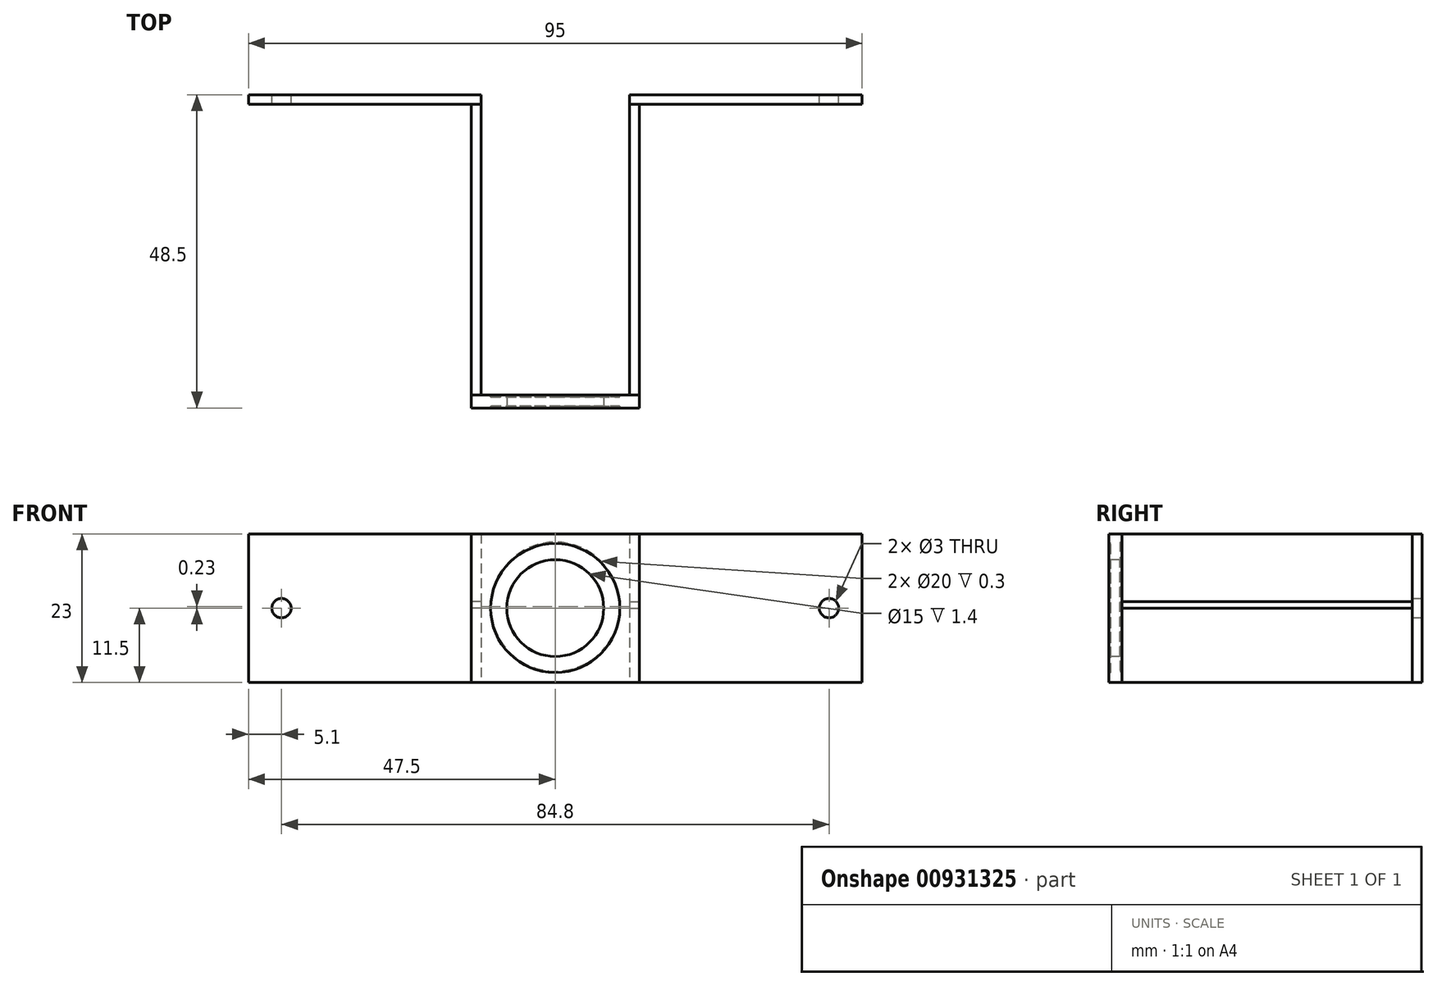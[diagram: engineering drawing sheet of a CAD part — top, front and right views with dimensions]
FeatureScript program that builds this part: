
annotation { "Feature Type Name" : "Feature", "Feature Type Description" : "" }
export const myFeature = defineFeature(function(context is Context, id is Id, definition is map)
    precondition{}
    {
        {
            var Q0;
            Q0=qCreatedBy(makeId("Front.planeOp"),FACE);
            var sketch = newSketch(context, id + "F0", { "sketchPlane" : qUnion([Q0])});
            skLineSegment(sketch, "E0.bottom", {"start": v(-47.5, 11.5) * mm, "end": v(47.5, 11.5) * mm});
            skLineSegment(sketch, "E0.top", {"start": v(-47.5, -11.5) * mm, "end": v(47.5, -11.5) * mm});
            skLineSegment(sketch, "E0.left", {"start": v(-47.5, 11.5) * mm, "end": v(-47.5, -11.5) * mm});
            skLineSegment(sketch, "E0.right", {"start": v(47.5, 11.5) * mm, "end": v(47.5, -11.5) * mm});
            skPoint(sketch, "E0.middle", {"position": v(0, 0) * mm});
            skCircle(sketch, "E1", {"center": v(-42.4, 0) * mm, "radius": 1.5 * mm});
            skCircle(sketch, "E2", {"center": v(42.4, 0) * mm, "radius": 1.5 * mm});
            skLineSegment(sketch, "E3.bottom", {"start": v(-11.5, 11.5) * mm, "end": v(11.5, 11.5) * mm});
            skLineSegment(sketch, "E3.top", {"start": v(-11.5, -11.5) * mm, "end": v(11.5, -11.5) * mm});
            skLineSegment(sketch, "E3.left", {"start": v(-11.5, 11.5) * mm, "end": v(-11.5, -11.5) * mm});
            skLineSegment(sketch, "E3.right", {"start": v(11.5, 11.5) * mm, "end": v(11.5, -11.5) * mm});
            skSolve(sketch);
        }
        {
            var Q0;
            {var subQ0=sQuery(id+"F0.wireOp",EDGE,"E0.left");Q0=makeQuery(id+"F0.imprint","IMPRINT",FACE,{"disambiguationData":[TD([[makeQuery(id+"F0.imprint","IMPRINT",EDGE,{"derivedFrom":subQ0}),1.0]])]});}
            var Q1;
            {var subQ0=sQuery(id+"F0.wireOp",EDGE,"E0.right");Q1=makeQuery(id+"F0.imprint","IMPRINT",FACE,{"disambiguationData":[TD([[makeQuery(id+"F0.imprint","IMPRINT",EDGE,{"derivedFrom":subQ0}),-1.0]])]});}
            extrude(context, id + "F1", {"entities" : qUnion([Q0, Q1]), "depth" : 1.5 * mm, "offsetDistance" : 25 * mm});
        }
        {
            var Q0;
            Q0=qCreatedBy(makeId("Top.planeOp"),FACE);
            var sketch = newSketch(context, id + "F2", { "sketchPlane" : qUnion([Q0])});
            skLineSegment(sketch, "E4.bottom", {"start": v(-11.5, -1.5) * mm, "end": v(-13, -1.5) * mm});
            skLineSegment(sketch, "E4.top", {"start": v(-11.5, -46.5) * mm, "end": v(-13, -46.5) * mm});
            skLineSegment(sketch, "E4.left", {"start": v(-11.5, -1.5) * mm, "end": v(-11.5, -46.5) * mm});
            skLineSegment(sketch, "E4.right", {"start": v(-13, -1.5) * mm, "end": v(-13, -46.5) * mm});
            skLineSegment(sketch, "E5.bottom", {"start": v(11.5, -1.5) * mm, "end": v(13, -1.5) * mm});
            skLineSegment(sketch, "E5.top", {"start": v(11.5, -46.5) * mm, "end": v(13, -46.5) * mm});
            skLineSegment(sketch, "E5.left", {"start": v(11.5, -1.5) * mm, "end": v(11.5, -46.5) * mm});
            skLineSegment(sketch, "E5.right", {"start": v(13, -1.5) * mm, "end": v(13, -46.5) * mm});
            skSolve(sketch);
        }
        {
            var Q0;
            Q0=makeQuery(id+"F2.imprint","IMPRINT",FACE,{"disambiguationData":[TD([[makeQuery(id+"F2.imprint","IMPRINT",EDGE,{"derivedFrom":sQuery(id+"F2.wireOp",EDGE,"E5.bottom")}),-1.0]])]});
            var Q1;
            Q1=makeQuery(id+"F2.imprint","IMPRINT",FACE,{"disambiguationData":[TD([[makeQuery(id+"F2.imprint","IMPRINT",EDGE,{"derivedFrom":sQuery(id+"F2.wireOp",EDGE,"E4.bottom")}),1.0]])]});
            extrude(context, id + "F3", {"entities" : qUnion([Q0, Q1]), "endBound" : BoundingType.SYMMETRIC, "depth" : 23 * mm, "offsetDistance" : 25 * mm});
        }
        {
            var Q0;
            Q0 = qSketchRegion(id + "F2", true);
            extrude(context, id + "F4", {"entities" : qUnion([Q0]), "depth" : 1 * mm, "offsetDistance" : 25 * mm});
        }
        {
            var Q0;
            Q0=makeQuery(id+"F3.opExtrude","SWEPT_FACE",FACE,{"disambiguationData":[OSD([sQuery(id+"F2.wireOp",EDGE,"E5.top")])]});
            var sketch = newSketch(context, id + "F5", { "sketchPlane" : qUnion([Q0])});
            skLineSegment(sketch, "E6.bottom", {"start": v(13, 11.5) * mm, "end": v(-13, 11.5) * mm});
            skLineSegment(sketch, "E6.top", {"start": v(13, -11.5) * mm, "end": v(-13, -11.5) * mm});
            skLineSegment(sketch, "E6.left", {"start": v(13, 11.5) * mm, "end": v(13, -11.5) * mm});
            skLineSegment(sketch, "E6.right", {"start": v(-13, 11.5) * mm, "end": v(-13, -11.5) * mm});
            skSolve(sketch);
        }
        {
            var Q0;
            Q0=makeQuery(id+"F5.imprint","IMPRINT",FACE,{"disambiguationData":[TD([[makeQuery(id+"F5.imprint","IMPRINT",EDGE,{"derivedFrom":sQuery(id+"F5.wireOp",EDGE,"E6.top")}),-1.0]])]});
            var Q1;
            {var subQ3=sQuery(id+"F5.wireOp",EDGE,"E6.left");Q1=makeQuery(id+"F5.imprint","IMPRINT",FACE,{"disambiguationData":[TD([[makeQuery(id+"F5.imprint","IMPRINT",EDGE,{"derivedFrom":subQ3}),-1.0]])]});}
            extrude(context, id + "F6", {"entities" : qUnion([Q0, Q1]), "depth" : 2 * mm, "offsetDistance" : 25 * mm});
        }
        {
            var Q0;
            Q0=makeQuery(id+"F6.opExtrude","CAP_FACE",FACE,{"disambiguationData":[OSD([sQuery(id+"F5.wireOp",EDGE,"E6.bottom"),sQuery(id+"F5.wireOp",EDGE,"E6.top"),sQuery(id+"F5.wireOp",EDGE,"E6.left"),sQuery(id+"F5.wireOp",EDGE,"E6.right")])],"isStart":false});
            var sketch = newSketch(context, id + "F7", { "sketchPlane" : qUnion([Q0])});
            skCircle(sketch, "E7", {"center": v(0, 0) * mm, "radius": 7.5 * mm});
            skCircle(sketch, "E8", {"center": v(0, 0) * mm, "radius": 10 * mm});
            skSolve(sketch);
        }
        {
            var Q0;
            Q0=makeQuery(id+"F7.imprint","IMPRINT",FACE,{"disambiguationData":[TD([[makeQuery(id+"F7.imprint","IMPRINT",EDGE,{"derivedFrom":sQuery(id+"F7.wireOp",EDGE,"E7")}),-1.0]])]});
            extrude(context, id + "F8", {"entities" : qUnion([Q0]), "operationType" : NewBodyOperationType.REMOVE, "oppositeDirection" : true, "depth" : .3 * mm, "offsetDistance" : 25 * mm});
        }
        {
            var Q0;
            Q0=makeQuery(id+"F8.boolean.opBoolean","SPLIT",FACE,{"disambiguationData":[TD([makeQuery(id+"F8.opExtrude","SWEPT_FACE",FACE,{"disambiguationData":[OSD([sQuery(id+"F7.wireOp",EDGE,"E7")])]})])],"derivedFrom":makeQuery(id+"F6.opExtrude","CAP_FACE",FACE,{"disambiguationData":[OSD([sQuery(id+"F5.wireOp",EDGE,"E6.bottom"),sQuery(id+"F5.wireOp",EDGE,"E6.top"),sQuery(id+"F5.wireOp",EDGE,"E6.left"),sQuery(id+"F5.wireOp",EDGE,"E6.right")])],"isStart":false})});
            extrude(context, id + "F9", {"entities" : qUnion([Q0]), "operationType" : NewBodyOperationType.REMOVE, "oppositeDirection" : true, "depth" : 2.2 * mm, "offsetDistance" : 25 * mm});
        }
        {
            var Q0;
            Q0=makeQuery(id+"F6.opExtrude","CAP_FACE",FACE,{"disambiguationData":[OSD([sQuery(id+"F5.wireOp",EDGE,"E6.bottom"),sQuery(id+"F5.wireOp",EDGE,"E6.top"),sQuery(id+"F5.wireOp",EDGE,"E6.left"),sQuery(id+"F5.wireOp",EDGE,"E6.right")])],"isStart":true});
            var sketch = newSketch(context, id + "F10", { "sketchPlane" : qUnion([Q0])});
            skCircle(sketch, "E9", {"center": v(0, 0.23) * mm, "radius": 10 * mm});
            skSolve(sketch);
        }
        {
            var Q0;
            Q0=makeQuery(id+"F10.imprint","IMPRINT",FACE,{"disambiguationData":[TD([[makeQuery(id+"F10.imprint","IMPRINT",EDGE,{"derivedFrom":sQuery(id+"F10.wireOp",EDGE,"E9")}),1.0]])]});
            extrude(context, id + "F11", {"entities" : qUnion([Q0]), "operationType" : NewBodyOperationType.REMOVE, "oppositeDirection" : true, "depth" : .3 * mm, "offsetDistance" : 25 * mm});
        }
    });
